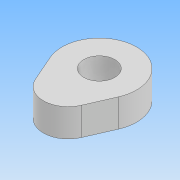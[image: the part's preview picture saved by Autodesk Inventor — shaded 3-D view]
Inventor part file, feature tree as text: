
AUTODESK INVENTOR PART (.ipt)
format: ipt  version: 2021 (Build 250183000, 183)  size: 90,624 bytes
history: native  units: mm
features: other x1, extrude x1, sketch x1
ambient origin geometry x8: Origin, YZ Plane, XZ Plane, XY Plane, X Axis, Y Axis, Z Axis, Center Point
bodies: Body1 (feature_tree)
feature tree (3):
  other  "實體1"
  extrude  "擠出1"  Depth=50.0mm
  sketch  "草圖1"
